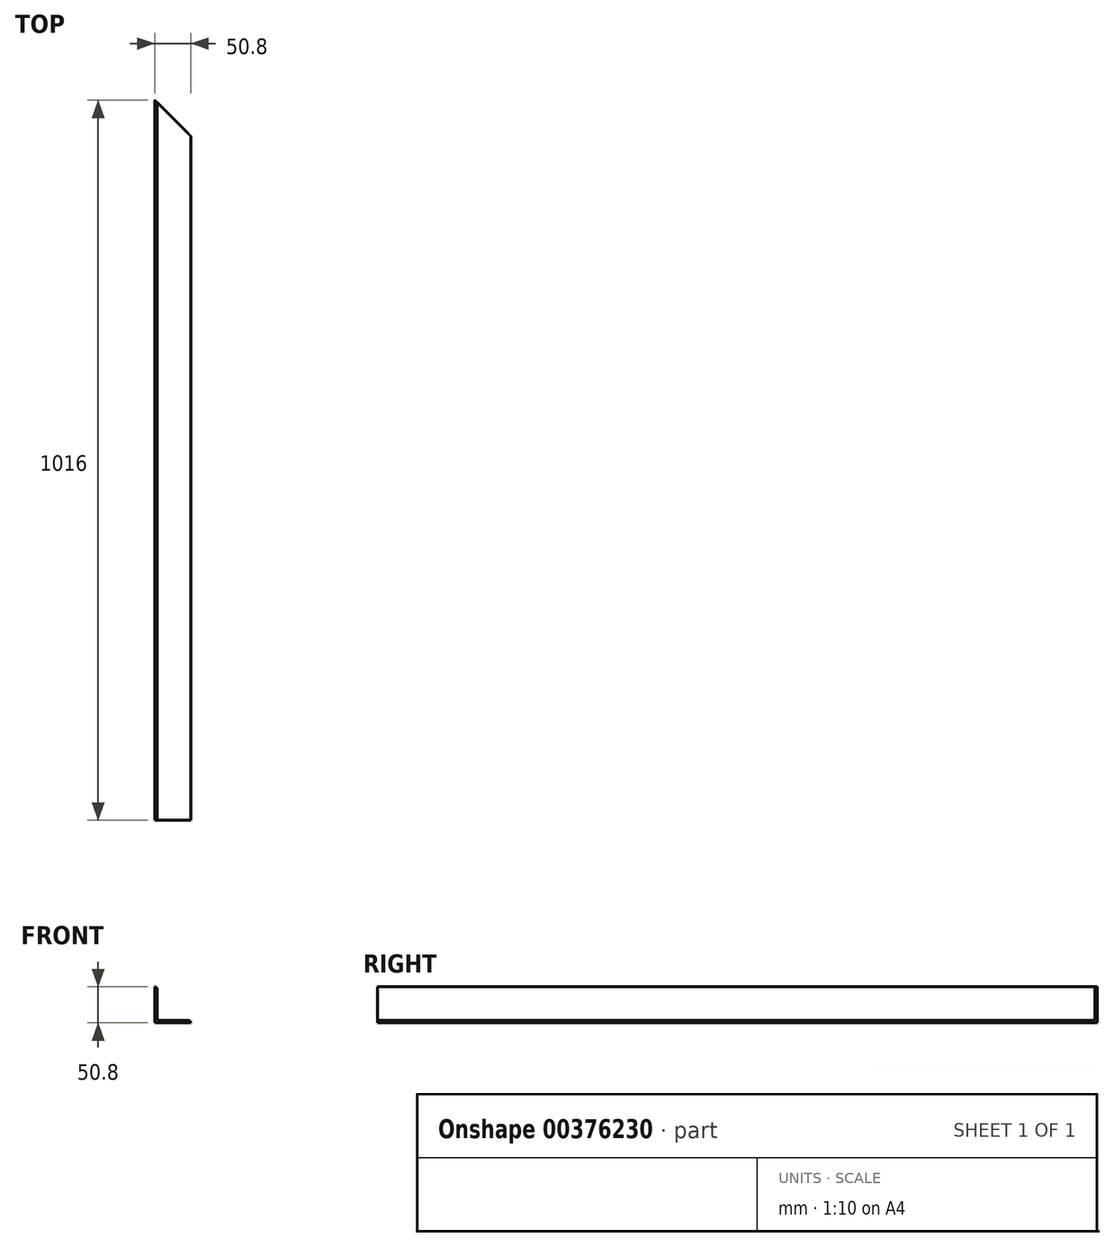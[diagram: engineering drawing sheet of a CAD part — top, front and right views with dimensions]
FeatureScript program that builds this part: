
annotation { "Feature Type Name" : "Feature", "Feature Type Description" : "" }
export const myFeature = defineFeature(function(context is Context, id is Id, definition is map)
    precondition{}
    {
        {
            var Q0;
            Q0=qCreatedBy(makeId("Front.planeOp"),FACE);
            var sketch = newSketch(context, id + "F0", { "sketchPlane" : qUnion([Q0])});
            skLineSegment(sketch, "E0", {"start": v(-923.93, 50.8) * mm, "end": v(-923.93, 0) * mm});
            skLineSegment(sketch, "E1", {"start": v(-873.13, 0) * mm, "end": v(-923.93, 0) * mm});
            skLineSegment(sketch, "E2.0", {"start": v(-876.3, 3.18) * mm, "end": v(-920.75, 3.18) * mm});
            skLineSegment(sketch, "E2.1", {"start": v(-920.75, 47.62) * mm, "end": v(-920.75, 3.18) * mm});
            skLineSegment(sketch, "E3", {"start": v(-923.93, 50.8) * mm, "end": v(-923.93, 50.8) * mm});
            skLineSegment(sketch, "E4", {"start": v(-873.13, 0) * mm, "end": v(-873.13, 0) * mm});
            skPoint(sketch, "E5.visualSharp", {"position": v(-920.75, 50.8) * mm});
            skArc(sketch, "E5.filletArc", {"start": v(-920.75, 47.62) * mm, "mid": v(-921.68, 49.87) * mm, "end": v(-923.93, 50.8) * mm});
            skPoint(sketch, "E6.visualSharp", {"position": v(-873.13, 3.18) * mm});
            skArc(sketch, "E6.filletArc", {"start": v(-873.13, 0) * mm, "mid": v(-874.05, 2.25) * mm, "end": v(-876.3, 3.17) * mm});
            skSolve(sketch);
        }
        {
            var Q0;
            Q0 = qSketchRegion(id + "F0", true);
            extrude(context, id + "F1", {"entities" : qUnion([Q0]), "endBound" : BoundingType.SYMMETRIC, "depth" : 1016 * mm});
        }
        {
            var Q0;
            Q0=makeQuery(id+"F1.opExtrude","SWEPT_FACE",FACE,{"disambiguationData":[OSD([sQuery(id+"F0.wireOp",EDGE,"E1")])]});
            var sketch = newSketch(context, id + "F2", { "sketchPlane" : qUnion([Q0])});
            skLineSegment(sketch, "E7", {"start": v(-923.93, -508) * mm, "end": v(-873.13, -508) * mm});
            skLineSegment(sketch, "E8", {"start": v(-873.13, -457.2) * mm, "end": v(-923.93, -508) * mm});
            skLineSegment(sketch, "E9", {"start": v(-873.13, -457.2) * mm, "end": v(-873.13, -508) * mm});
            skSolve(sketch);
        }
        {
            var Q0;
            Q0 = qSketchRegion(id + "F2", true);
            extrude(context, id + "F3", {"entities" : qUnion([Q0]), "operationType" : NewBodyOperationType.REMOVE, "oppositeDirection" : true, "depth" : 50.8 * mm});
        }
    });
